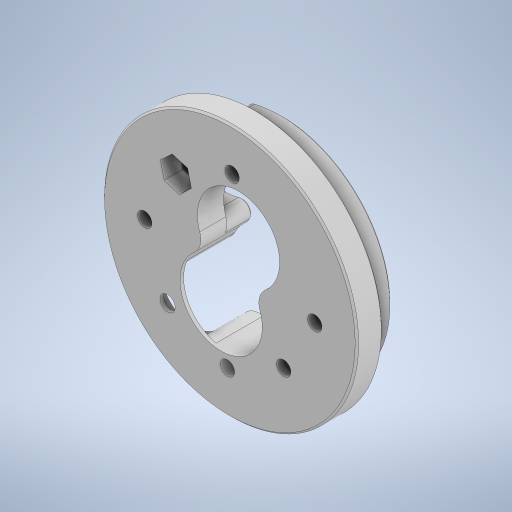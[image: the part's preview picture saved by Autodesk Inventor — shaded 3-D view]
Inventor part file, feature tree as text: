
AUTODESK INVENTOR PART (.ipt)
format: ipt  version: 2023 (Build 270158000, 158)  size: 994,816 bytes
history: native  units: in
note: dims shown in document units (in); Inventor stores cm internally (conversion verified against a paired STEP export)
features: extrude x6, sketch x4, projected_geometry x4, other x3, chamfer x2, fillet x2, reference x2
ambient origin geometry x8: Origin, YZ Plane, XZ Plane, XY Plane, X Axis, Y Axis, Z Axis, Center Point
bodies: Solid1 (feature_tree)
feature tree (23):
  extrude  "Extrusion1"  Depth=0.9in
  extrude  "Extrusion2"  Depth=0.35in
  chamfer  "Chamfer1"  Distance=0.35in
  fillet  "Fillet1"  Radius=3.4in
  extrude  "Extrusion3"  Depth=0.35in
  extrude  "Extrusion4"  Depth=0.25in
  extrude  "Extrusion5"  Depth=0.125in
  extrude  "Extrusion6"  Depth=0.1in TaperAngle=0.0deg
  fillet  "Fillet2"  Radius=0.33in
  chamfer  "Chamfer2"  Distance=0.1in
  sketch  "Sketch1"  dims[d0=1.1in d1=0.9in]
  reference  "Reference1"
  projected_geometry  "Projected Loop1"
  sketch  "Sketch3"  dims[d2=0.0098in d3=2.95in d4=0.35in d5=0.0in d6=3.4in]
  projected_geometry  "Projected Loop2"
  reference  "Reference2"
  sketch  "Sketch5"  dims[d7=0.35in d8=0.0in d11=0.19in]
  projected_geometry  "Projected Loop3"
  sketch  "Sketch6"  dims[d12=0.0236in d13=0.125in d14=45.0deg d15=0.25in d16=0.19in d17=0.1in d18=0.0in d19=0.33in d20=0.1in d21=0.0in d22=0.375in d23=0.19in d24=0.1in d25=0.0in d26=0.0472in d27=0.0in d28=0.125in d29=0.2in d30=0.0236in d31=0.125in d32=45.0deg d9=0.5in d10=0.0344in]
  projected_geometry  "Projected Loop4"
  other  "<userpath>\Documents\CAD\guardSwerve5\MainAssy.iam"
  other  "MainAssy.iam"
  other  "SteeringCoupler:1"
